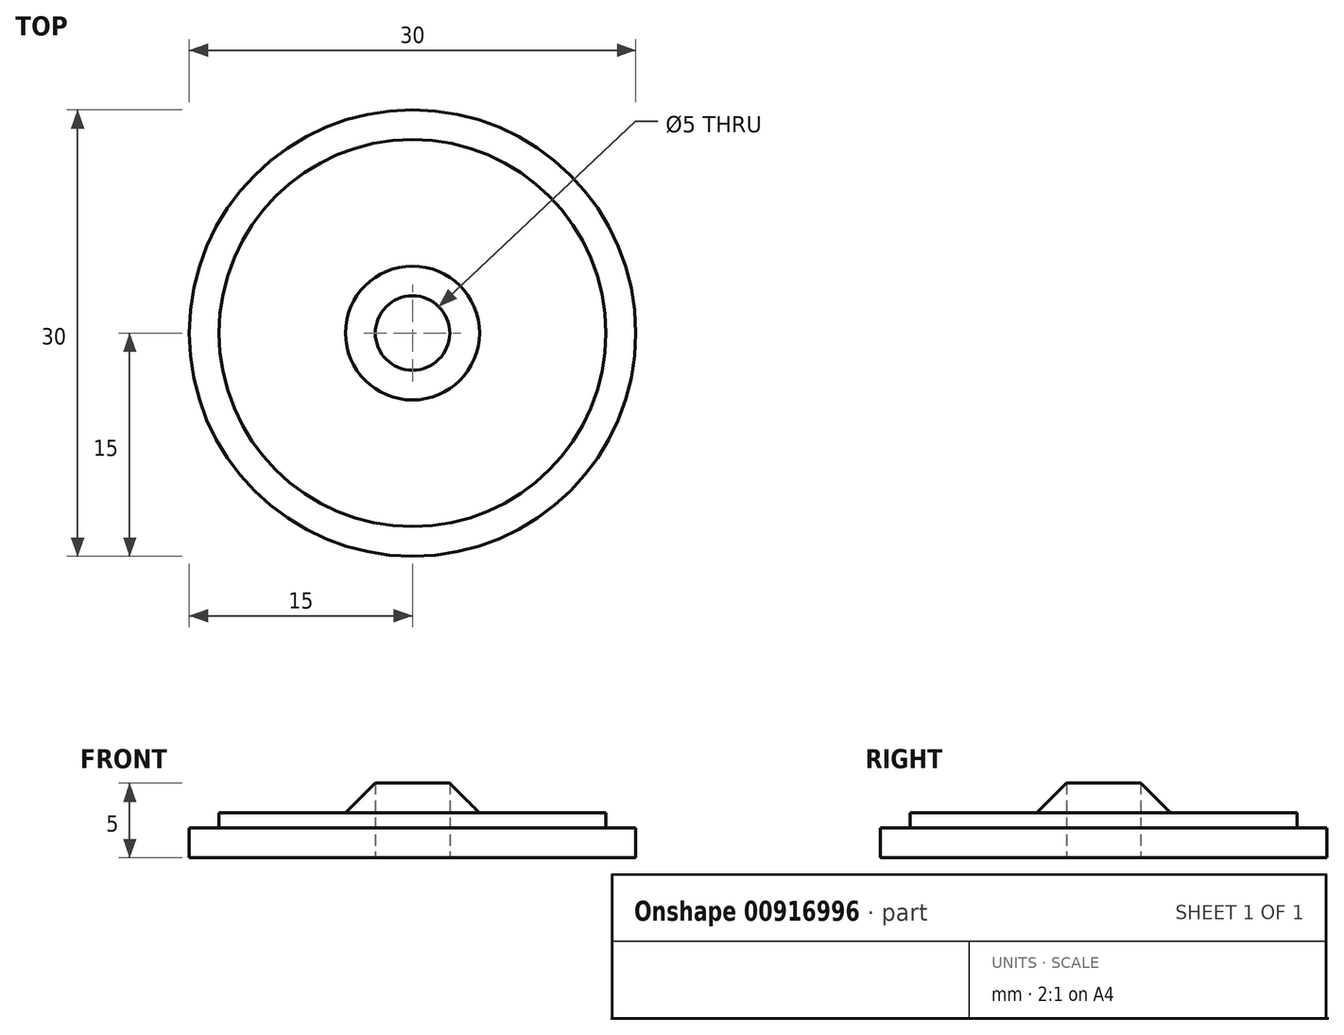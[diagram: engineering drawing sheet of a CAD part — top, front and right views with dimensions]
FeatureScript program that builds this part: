
annotation { "Feature Type Name" : "Feature", "Feature Type Description" : "" }
export const myFeature = defineFeature(function(context is Context, id is Id, definition is map)
    precondition{}
    {
        {
            var Q0;
            Q0=qCreatedBy(makeId("Top.planeOp"),FACE);
            var sketch = newSketch(context, id + "F0", { "sketchPlane" : qUnion([Q0])});
            skCircle(sketch, "E0", {"center": v(0, 0) * mm, "radius": 15 * mm});
            skCircle(sketch, "E1", {"center": v(0, 0) * mm, "radius": 2.5 * mm});
            skSolve(sketch);
        }
        {
            var Q0;
            Q0=makeQuery(id+"F0.imprint","IMPRINT",FACE,{"disambiguationData":[TD([[makeQuery(id+"F0.imprint","IMPRINT",EDGE,{"derivedFrom":sQuery(id+"F0.wireOp",EDGE,"E0")}),1.0]])]});
            extrude(context, id + "F1", {"entities" : qUnion([Q0]), "depth" : 2 * mm, "offsetDistance" : 25 * mm});
        }
        {
            var Q0;
            Q0=makeQuery(id+"F1.opExtrude","CAP_FACE",FACE,{"disambiguationData":[OSD([sQuery(id+"F0.wireOp",EDGE,"E0"),sQuery(id+"F0.wireOp",EDGE,"E1")])],"isStart":false});
            var sketch = newSketch(context, id + "F2", { "sketchPlane" : qUnion([Q0])});
            skCircle(sketch, "E2", {"center": v(0, 0) * mm, "radius": 13 * mm});
            skSolve(sketch);
        }
        {
            var Q0;
            Q0=makeQuery(id+"F2.imprint","IMPRINT",FACE,{"disambiguationData":[TD([[makeQuery(id+"F2.imprint","IMPRINT",EDGE,{"derivedFrom":sQuery(id+"F2.wireOp",EDGE,"E2")}),1.0]])]});
            extrude(context, id + "F3", {"entities" : qUnion([Q0]), "operationType" : NewBodyOperationType.ADD, "depth" : 1 * mm, "offsetDistance" : 25 * mm});
        }
        {
            var Q0;
            Q0=makeQuery(id+"F3.opExtrude","CAP_FACE",FACE,{"disambiguationData":[OSD([sQuery(id+"F0.wireOp",EDGE,"E1"),sQuery(id+"F2.wireOp",EDGE,"E2")])],"isStart":false});
            var sketch = newSketch(context, id + "F4", { "sketchPlane" : qUnion([Q0])});
            skCircle(sketch, "E3", {"center": v(0, 0) * mm, "radius": 4.5 * mm});
            skSolve(sketch);
        }
        {
            var Q0;
            Q0=makeQuery(id+"F4.imprint","IMPRINT",FACE,{"disambiguationData":[TD([[makeQuery(id+"F4.imprint","IMPRINT",EDGE,{"derivedFrom":sQuery(id+"F4.wireOp",EDGE,"E3")}),1.0]])]});
            extrude(context, id + "F5", {"entities" : qUnion([Q0]), "operationType" : NewBodyOperationType.ADD, "depth" : 2 * mm, "offsetDistance" : 25 * mm});
        }
        {
            var Q0;
            Q0=makeQuery(id+"F5.opExtrude","CAP_EDGE",EDGE,{"disambiguationData":[OSD([sQuery(id+"F4.wireOp",EDGE,"E3")])],"isStart":false});
            chamfer(context, id + "F6", {"entities" : qUnion([Q0]), "chamferType" : ChamferType.TWO_OFFSETS, "width1" : 2 * mm, "oppositeDirection" : false, "width2" : 2 * mm, "tangentPropagation" : true});
        }
    });
